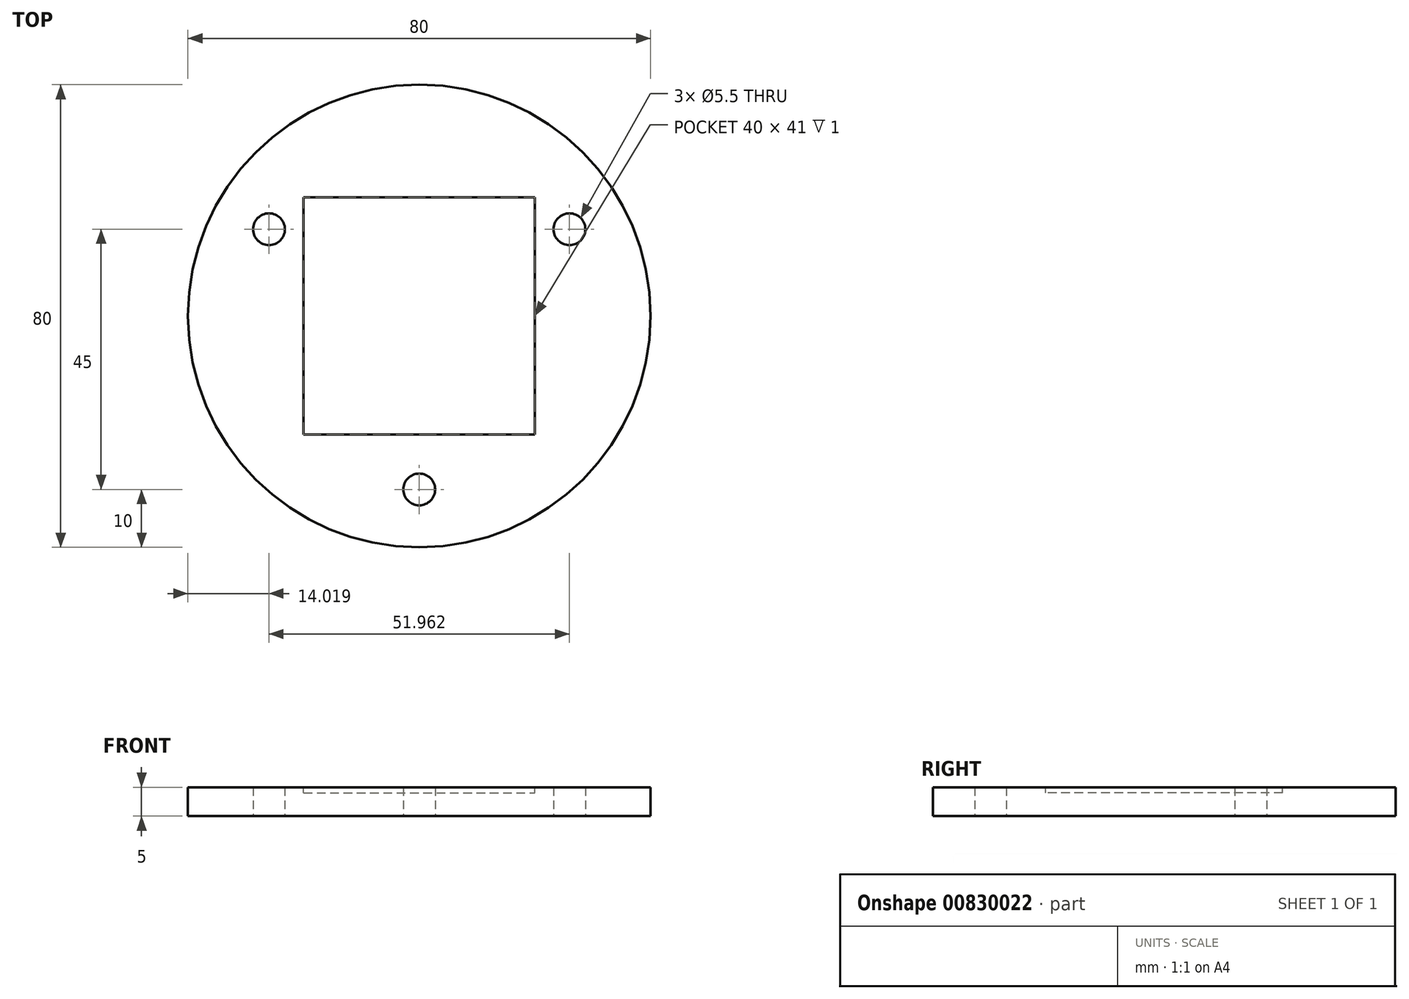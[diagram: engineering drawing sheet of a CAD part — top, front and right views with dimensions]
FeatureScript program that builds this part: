
annotation { "Feature Type Name" : "Feature", "Feature Type Description" : "" }
export const myFeature = defineFeature(function(context is Context, id is Id, definition is map)
    precondition{}
    {
        {
            var Q0;
            Q0=qCreatedBy(makeId("Top.planeOp"),FACE);
            var sketch = newSketch(context, id + "F0", { "sketchPlane" : qUnion([Q0])});
            skCircle(sketch, "E0", {"center": v(0, 0) * mm, "radius": 40 * mm});
            skSolve(sketch);
        }
        {
            var Q0;
            Q0=makeQuery(id+"F0.imprint","IMPRINT",FACE,{"disambiguationData":[TD([[makeQuery(id+"F0.imprint","IMPRINT",EDGE,{"derivedFrom":sQuery(id+"F0.wireOp",EDGE,"E0")}),1.0]])]});
            extrude(context, id + "F1", {"entities" : qUnion([Q0]), "depth" : 5 * mm, "offsetDistance" : 25 * mm});
        }
        {
            var Q0;
            Q0=makeQuery(id+"F1.opExtrude","CAP_FACE",FACE,{"disambiguationData":[OSD([sQuery(id+"F0.wireOp",EDGE,"E0")])],"isStart":false});
            var sketch = newSketch(context, id + "F2", { "sketchPlane" : qUnion([Q0])});
            skLineSegment(sketch, "E1.bottom", {"start": v(-20, 20.5) * mm, "end": v(20, 20.5) * mm});
            skLineSegment(sketch, "E1.top", {"start": v(-20, -20.5) * mm, "end": v(20, -20.5) * mm});
            skLineSegment(sketch, "E1.left", {"start": v(-20, 20.5) * mm, "end": v(-20, -20.5) * mm});
            skLineSegment(sketch, "E1.right", {"start": v(20, 20.5) * mm, "end": v(20, -20.5) * mm});
            skSolve(sketch);
        }
        {
            var Q0;
            Q0 = qSketchRegion(id + "F2", true);
            extrude(context, id + "F3", {"entities" : qUnion([Q0]), "operationType" : NewBodyOperationType.REMOVE, "oppositeDirection" : true, "depth" : 1 * mm, "offsetDistance" : 25 * mm});
        }
        {
            var Q0;
            Q0=makeQuery(id+"F1.opExtrude","CAP_FACE",FACE,{"disambiguationData":[OSD([sQuery(id+"F0.wireOp",EDGE,"E0")])],"isStart":true});
            var sketch = newSketch(context, id + "F4", { "sketchPlane" : qUnion([Q0])});
            skCircle(sketch, "E2", {"center": v(0, 0) * mm, "radius": 30 * mm, "construction": true});
            skPoint(sketch, "E3", {"position": v(0, 30) * mm});
            skLineSegment(sketch, "E4", {"start": v(0, 0) * mm, "end": v(0, 30) * mm, "construction": true});
            skLineSegment(sketch, "E5", {"start": v(0, 0) * mm, "end": v(25.98, -15) * mm, "construction": true});
            skLineSegment(sketch, "E6", {"start": v(-25.98, -15) * mm, "end": v(0, 0) * mm, "construction": true});
            skSolve(sketch);
        }
        {
            var Q0;
            Q0=sQuery(id+"F4.wireOp",VERTEX,"E3");
            var Q1;
            Q1=sQuery(id+"F4.wireOp",VERTEX,"E5.end");
            var Q2;
            Q2=sQuery(id+"F4.wireOp",VERTEX,"E6.start");
            var Q3;
            Q3=makeQuery(id+"F1.opExtrude","SWEPT_BODY",BODY,{"disambiguationData":[OSD([sQuery(id+"F0.wireOp",EDGE,"E0")])]});
            hole(context, id + "F5", {"style" : HoleStyle.SIMPLE, "endStyle" : HoleEndStyle.THROUGH, "holeDiameter" : 5.5 * mm, "majorDiameter" : 5 * mm, "isTappedThrough" : true, "tappedDepth" : 12 * mm, "tapClearance" : 3, "locations" : qUnion([Q0, Q1, Q2]), "scope" : qUnion([Q3])});
        }
        {
            var Q0;
            Q0=makeQuery(id+"F2.imprint","IMPRINT",FACE,{"disambiguationData":[TD([[makeQuery(id+"F2.imprint","IMPRINT",EDGE,{"derivedFrom":sQuery(id+"F2.wireOp",EDGE,"E1.bottom")}),-1.0]])]});
            extrude(context, id + "F6", {"entities" : qUnion([Q0]), "operationType" : NewBodyOperationType.REMOVE, "oppositeDirection" : true, "depth" : 1 * mm, "offsetDistance" : 25 * mm});
        }
    });
